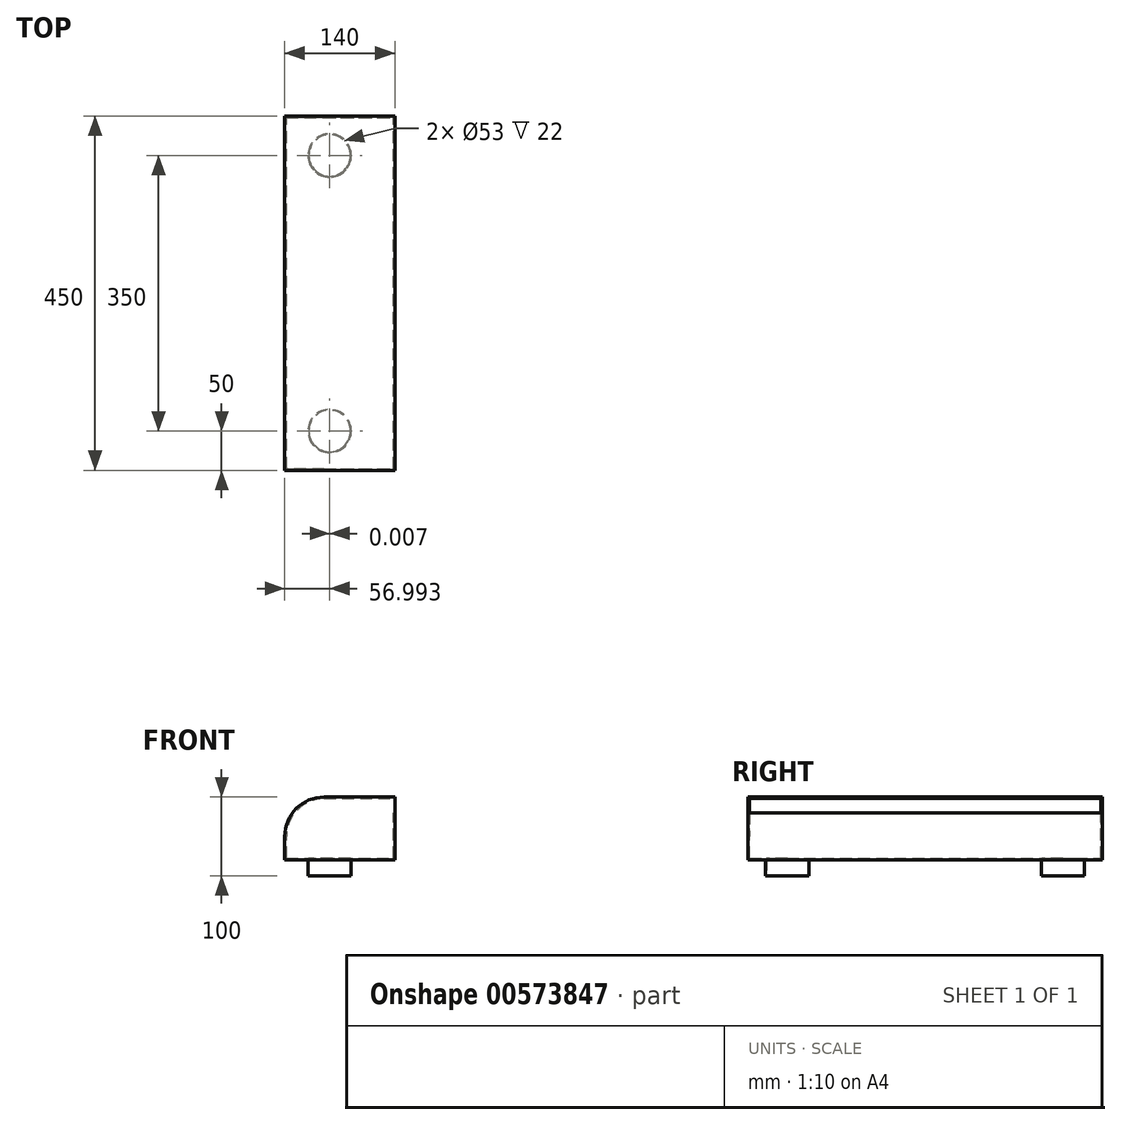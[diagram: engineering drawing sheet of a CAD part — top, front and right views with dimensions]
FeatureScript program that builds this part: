
annotation { "Feature Type Name" : "Feature", "Feature Type Description" : "" }
export const myFeature = defineFeature(function(context is Context, id is Id, definition is map)
    precondition{}
    {
        {
            var Q0;
            Q0=qCreatedBy(makeId("Front.planeOp"),FACE);
            var sketch = newSketch(context, id + "F0", { "sketchPlane" : qUnion([Q0])});
            skLineSegment(sketch, "E0.bottom", {"start": v(0, 0) * mm, "end": v(140, 0) * mm});
            skLineSegment(sketch, "E0.top", {"start": v(50, 80) * mm, "end": v(140, 80) * mm});
            skLineSegment(sketch, "E0.left", {"start": v(0, 0) * mm, "end": v(0, 30) * mm});
            skLineSegment(sketch, "E0.right", {"start": v(140, 0) * mm, "end": v(140, 80) * mm});
            skPoint(sketch, "E1.visualSharp", {"position": v(0, 80) * mm});
            skArc(sketch, "E1.filletArc", {"start": v(50, 80) * mm, "mid": v(14.64, 65.36) * mm, "end": v(0, 30) * mm});
            skSolve(sketch);
        }
        {
            var Q0;
            Q0 = qSketchRegion(id + "F0", true);
            extrude(context, id + "F1", {"entities" : qUnion([Q0]), "endBound" : BoundingType.SYMMETRIC, "depth" : 450 * mm, "offsetDistance" : 25.4 * mm});
        }
        {
            var Q0;
            Q0=makeQuery(id+"F1.opExtrude","SWEPT_FACE",FACE,{"disambiguationData":[OSD([sQuery(id+"F0.wireOp",EDGE,"E0.right")])]});
            shell(context, id + "F2", {"entities" : qUnion([Q0]), "thickness" : 2 * mm});
        }
        {
            var Q0;
            {var subQ0=sQuery(id+"F0.wireOp",EDGE,"E1.filletArc");var subQ1=sQuery(id+"F0.wireOp",EDGE,"E0.right");var subQ2=sQuery(id+"F0.wireOp",EDGE,"E0.left");var subQ3=sQuery(id+"F0.wireOp",EDGE,"E0.top");var subQ4=sQuery(id+"F0.wireOp",EDGE,"E0.bottom");Q0=makeQuery(id+"F2.opShell","OFFSET_FACE",FACE,{"disambiguationData":[OSD([subQ4,subQ3,subQ2,subQ1,subQ0]),TDD([makeQuery(id+"F1.opExtrude","CAP_FACE",FACE,{"disambiguationData":[OSD([subQ4,subQ3,subQ2,subQ1,subQ0])],"isStart":true})])]});}
            var sketch = newSketch(context, id + "F3", { "sketchPlane" : qUnion([Q0])});
            skLineSegment(sketch, "E2.bottom", {"start": v(140, 2) * mm, "end": v(138, 2) * mm});
            skLineSegment(sketch, "E2.top", {"start": v(140, 60) * mm, "end": v(138, 60) * mm});
            skLineSegment(sketch, "E2.left", {"start": v(140, 2) * mm, "end": v(140, 60) * mm});
            skLineSegment(sketch, "E2.right", {"start": v(138, 2) * mm, "end": v(138, 60) * mm});
            skSolve(sketch);
        }
        {
            var Q0;
            Q0 = qSketchRegion(id + "F3", true);
            var Q1;
            {var subQ0=sQuery(id+"F0.wireOp",EDGE,"E1.filletArc");var subQ1=sQuery(id+"F0.wireOp",EDGE,"E0.right");var subQ2=sQuery(id+"F0.wireOp",EDGE,"E0.left");var subQ3=sQuery(id+"F0.wireOp",EDGE,"E0.top");var subQ4=sQuery(id+"F0.wireOp",EDGE,"E0.bottom");Q1=makeQuery(id+"F2.opShell","OFFSET_FACE",FACE,{"disambiguationData":[OSD([subQ4,subQ3,subQ2,subQ1,subQ0]),TDD([makeQuery(id+"F1.opExtrude","CAP_FACE",FACE,{"disambiguationData":[OSD([subQ4,subQ3,subQ2,subQ1,subQ0])],"isStart":false})])]});}
            extrude(context, id + "F4", {"entities" : qUnion([Q0]), "operationType" : NewBodyOperationType.ADD, "endBound" : BoundingType.UP_TO_SURFACE, "depth" : 25.4 * mm, "endBoundEntityFace" : qUnion([Q1]), "offsetDistance" : 25.4 * mm});
        }
        {
            var Q0;
            Q0=makeQuery(id+"F1.opExtrude","SWEPT_FACE",FACE,{"disambiguationData":[OSD([sQuery(id+"F0.wireOp",EDGE,"E0.bottom")])]});
            var sketch = newSketch(context, id + "F5", { "sketchPlane" : qUnion([Q0])});
            skCircle(sketch, "E3", {"center": v(57, 175) * mm, "radius": 26.5 * mm});
            skCircle(sketch, "E4", {"center": v(57, -175) * mm, "radius": 26.5 * mm});
            skSolve(sketch);
        }
        {
            var Q0;
            Q0=makeQuery(id+"F5.imprint","IMPRINT",FACE,{"disambiguationData":[TD([[makeQuery(id+"F5.imprint","IMPRINT",EDGE,{"derivedFrom":sQuery(id+"F5.wireOp",EDGE,"E3")}),1.0]])]});
            var Q1;
            Q1=makeQuery(id+"F5.imprint","IMPRINT",FACE,{"disambiguationData":[TD([[makeQuery(id+"F5.imprint","IMPRINT",EDGE,{"derivedFrom":sQuery(id+"F5.wireOp",EDGE,"E4")}),1.0]])]});
            var Q2;
            Q2=sQuery(id+"F5.wireOp",EDGE,"E3");
            var Q3;
            Q3=sQuery(id+"F5.wireOp",EDGE,"E4");
            extrude(context, id + "F6", {"entities" : qUnion([Q0, Q1]), "operationType" : NewBodyOperationType.REMOVE, "surfaceEntities" : qUnion([Q2, Q3]), "oppositeDirection" : true, "depth" : 25.4 * mm, "offsetDistance" : 25.4 * mm});
        }
        {
            var Q0;
            Q0=makeQuery(id+"F1.opExtrude","SWEPT_FACE",FACE,{"disambiguationData":[OSD([sQuery(id+"F0.wireOp",EDGE,"E0.bottom")])]});
            var sketch = newSketch(context, id + "F7", { "sketchPlane" : qUnion([Q0])});
            skCircle(sketch, "E5", {"center": v(57, 175) * mm, "radius": 27.5 * mm});
            skCircle(sketch, "E6.0", {"center": v(57, 175) * mm, "radius": 26.5 * mm});
            skCircle(sketch, "E7.0", {"center": v(57, -175) * mm, "radius": 26.5 * mm});
            skCircle(sketch, "E8", {"center": v(57, -175) * mm, "radius": 27.5 * mm});
            skSolve(sketch);
        }
        {
            var Q0;
            Q0 = qSketchRegion(id + "F7", true);
            extrude(context, id + "F8", {"entities" : qUnion([Q0]), "operationType" : NewBodyOperationType.ADD, "depth" : 20 * mm, "offsetDistance" : 25.4 * mm});
        }
    });
